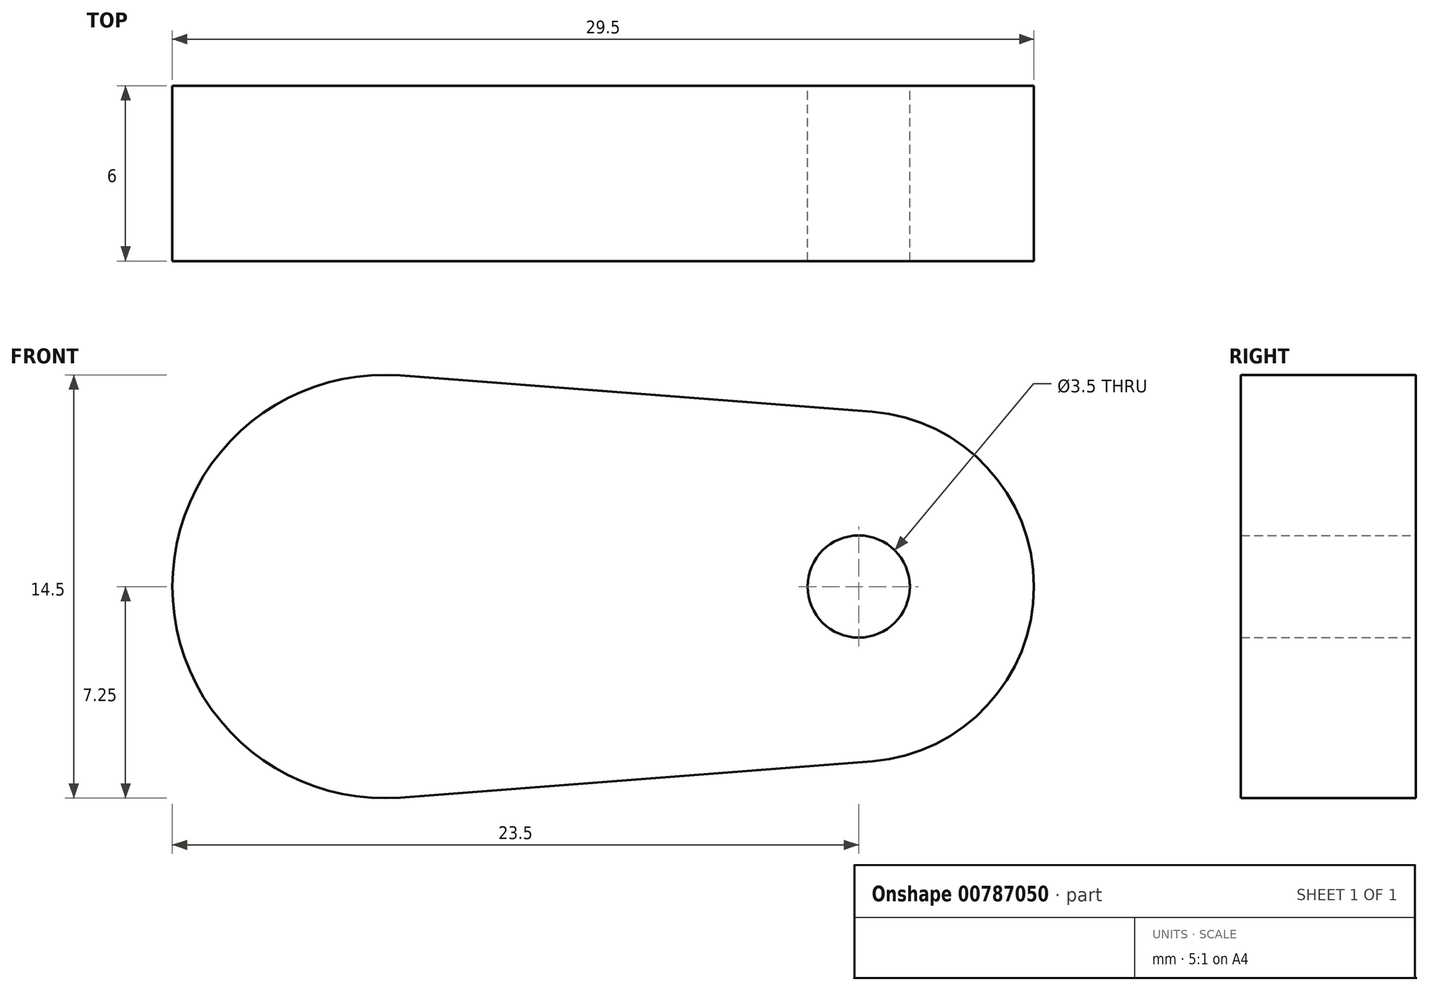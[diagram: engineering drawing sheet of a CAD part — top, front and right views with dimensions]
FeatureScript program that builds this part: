
annotation { "Feature Type Name" : "Feature", "Feature Type Description" : "" }
export const myFeature = defineFeature(function(context is Context, id is Id, definition is map)
    precondition{}
    {
        {
            var Q0;
            Q0=qCreatedBy(makeId("Front.planeOp"),FACE);
            var sketch = newSketch(context, id + "F0", { "sketchPlane" : qUnion([Q0])});
            skCircle(sketch, "E0", {"center": v(0, 0) * mm, "radius": 1.75 * mm});
            skArc(sketch, "E1", {"start": v(0.46, -5.98) * mm, "mid": v(6, 0) * mm, "end": v(0.46, 5.98) * mm});
            skArc(sketch, "E2", {"start": v(-15.7, 7.23) * mm, "mid": v(-23.5, 0) * mm, "end": v(-15.7, -7.23) * mm});
            skLineSegment(sketch, "E3", {"start": v(0, 0) * mm, "end": v(-16.25, 0) * mm, "construction": true});
            skLineSegment(sketch, "E4", {"start": v(-15.7, -7.23) * mm, "end": v(0.46, -5.98) * mm});
            skLineSegment(sketch, "E5.MirrorCS", {"start": v(-15.7, 7.23) * mm, "end": v(0.46, 5.98) * mm});
            skSolve(sketch);
        }
        {
            var Q0;
            Q0 = qSketchRegion(id + "F0", true);
            extrude(context, id + "F1", {"entities" : qUnion([Q0]), "endBound" : BoundingType.SYMMETRIC, "depth" : 6 * mm, "offsetDistance" : 25 * mm});
        }
    });
